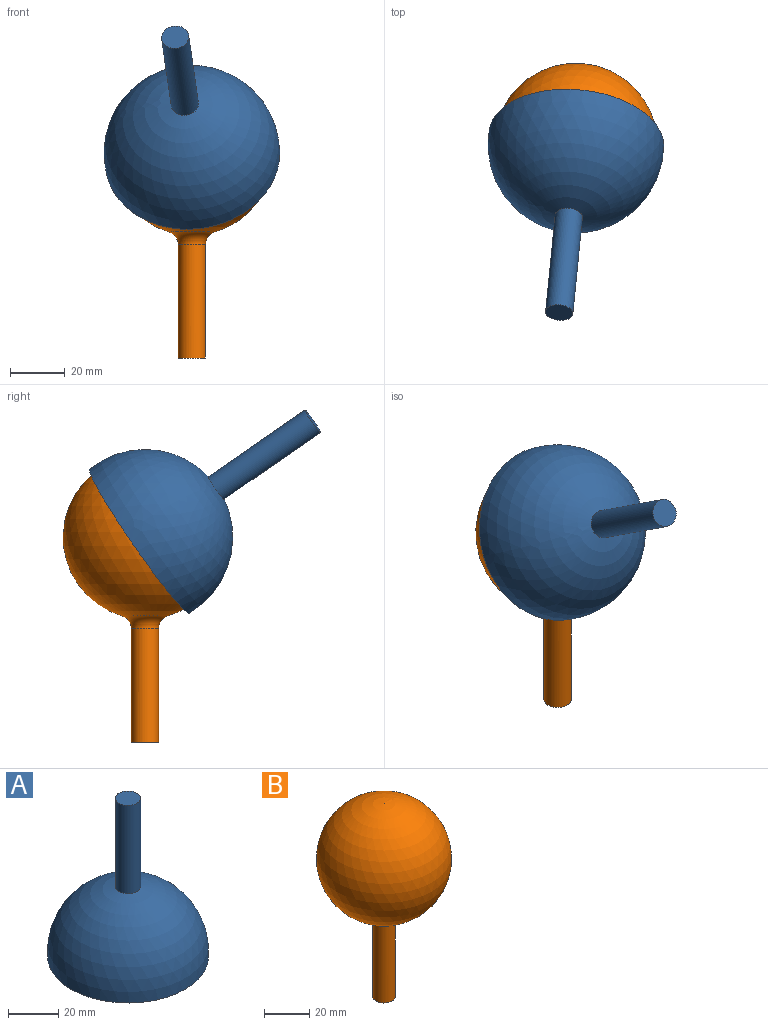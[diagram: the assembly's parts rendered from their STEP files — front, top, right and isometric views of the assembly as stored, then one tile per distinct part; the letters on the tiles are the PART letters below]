
ASSEMBLY  parts=2 mates=1
PART A: 5 faces, bbox 64.4x64.4x77.4 mm
  f0: sphere r=30.2mm, area 6190.7mm2, adj f1
  f1: plane 64.22x64.22mm, normal (0,0,-1), area 392.1mm2, adj f0,f2
  f2: sphere r=32.2mm, area 6926.3mm2, adj f1,f3
  f3: cylinder r=5mm len=43.19mm, axis (0,0,1), area 1356.9mm2, adj f2,f4
  f4: plane 10x10mm, normal (0,0,1), area 78.5mm2, adj f3
PART B: 4 faces, bbox 60x60x105 mm
  f0: cylinder r=5mm len=41.46mm, axis (0,0,-1), area 1302.5mm2, adj f2,f3
  f1: sphere r=30mm, area 11074mm2, adj f3
  f2: plane 10x10mm, normal (0,0,-1), area 78.5mm2, adj f0
  f3: torus R=10mm, axis (0,0,1), area 251.9mm2, adj f0,f1
PLACE A rot(axis=(0,-0.47,0.88),169.4deg) t=(0,0,75)mm
PLACE B t=(0,0,75)mm
MATE ball B.f0 <-> A.f3  axis (0,0,1) through (0,0,75)mm
